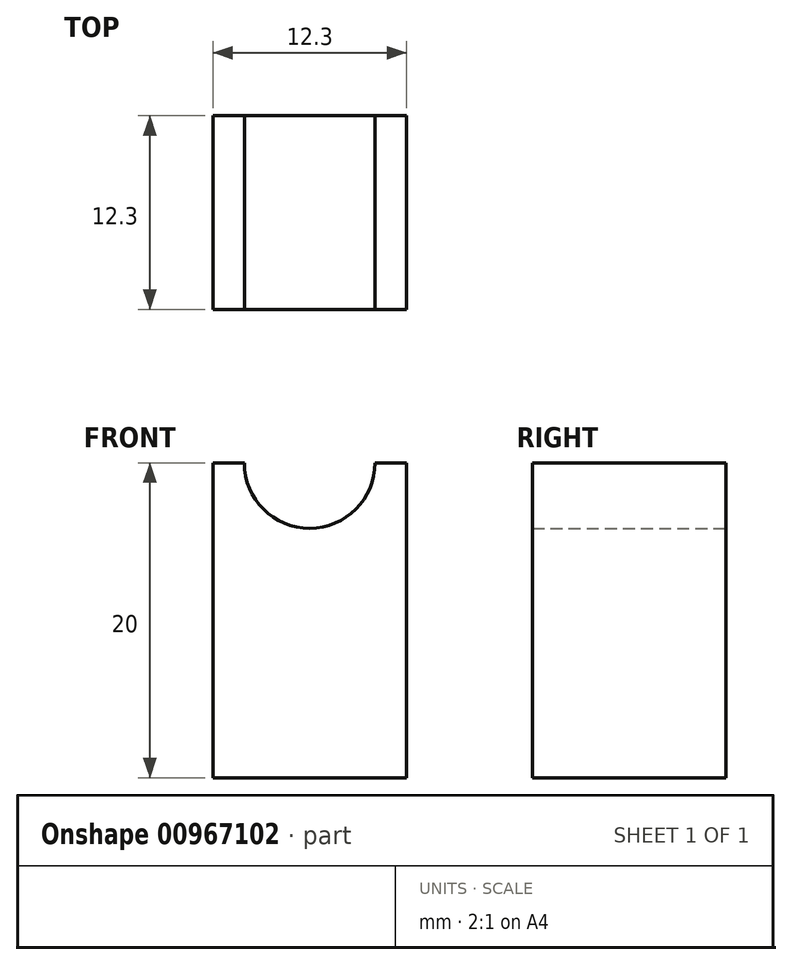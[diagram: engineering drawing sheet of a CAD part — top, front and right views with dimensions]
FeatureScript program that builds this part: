
annotation { "Feature Type Name" : "Feature", "Feature Type Description" : "" }
export const myFeature = defineFeature(function(context is Context, id is Id, definition is map)
    precondition{}
    {
        {
            var Q0;
            Q0=qCreatedBy(makeId("Front.planeOp"),FACE);
            var sketch = newSketch(context, id + "F0", { "sketchPlane" : qUnion([Q0])});
            skLineSegment(sketch, "E0.bottom", {"start": v(6.15, 10) * mm, "end": v(4.15, 10) * mm});
            skLineSegment(sketch, "E0.top", {"start": v(6.15, -10) * mm, "end": v(-6.15, -10) * mm});
            skLineSegment(sketch, "E0.left", {"start": v(6.15, 10) * mm, "end": v(6.15, -10) * mm});
            skLineSegment(sketch, "E0.right", {"start": v(-6.15, 10) * mm, "end": v(-6.15, -10) * mm});
            skPoint(sketch, "E0.middle", {"position": v(0, 0) * mm});
            skArc(sketch, "E1", {"start": v(-4.15, 10) * mm, "mid": v(0, 5.85) * mm, "end": v(4.15, 10) * mm});
            skLineSegment(sketch, "E2.trimOffspring", {"start": v(-4.15, 10) * mm, "end": v(-6.15, 10) * mm});
            skPoint(sketch, "E3.orphan", {"position": v(0, -10) * mm});
            skSolve(sketch);
        }
        {
            var Q0;
            Q0=makeQuery(id+"F0.imprint","IMPRINT",FACE,{"disambiguationData":[TD([[makeQuery(id+"F0.imprint","IMPRINT",EDGE,{"derivedFrom":sQuery(id+"F0.wireOp",EDGE,"E0.bottom")}),1.0]])]});
            extrude(context, id + "F1", {"entities" : qUnion([Q0]), "depth" : 12.3 * mm, "offsetDistance" : 25 * mm});
        }
    });
